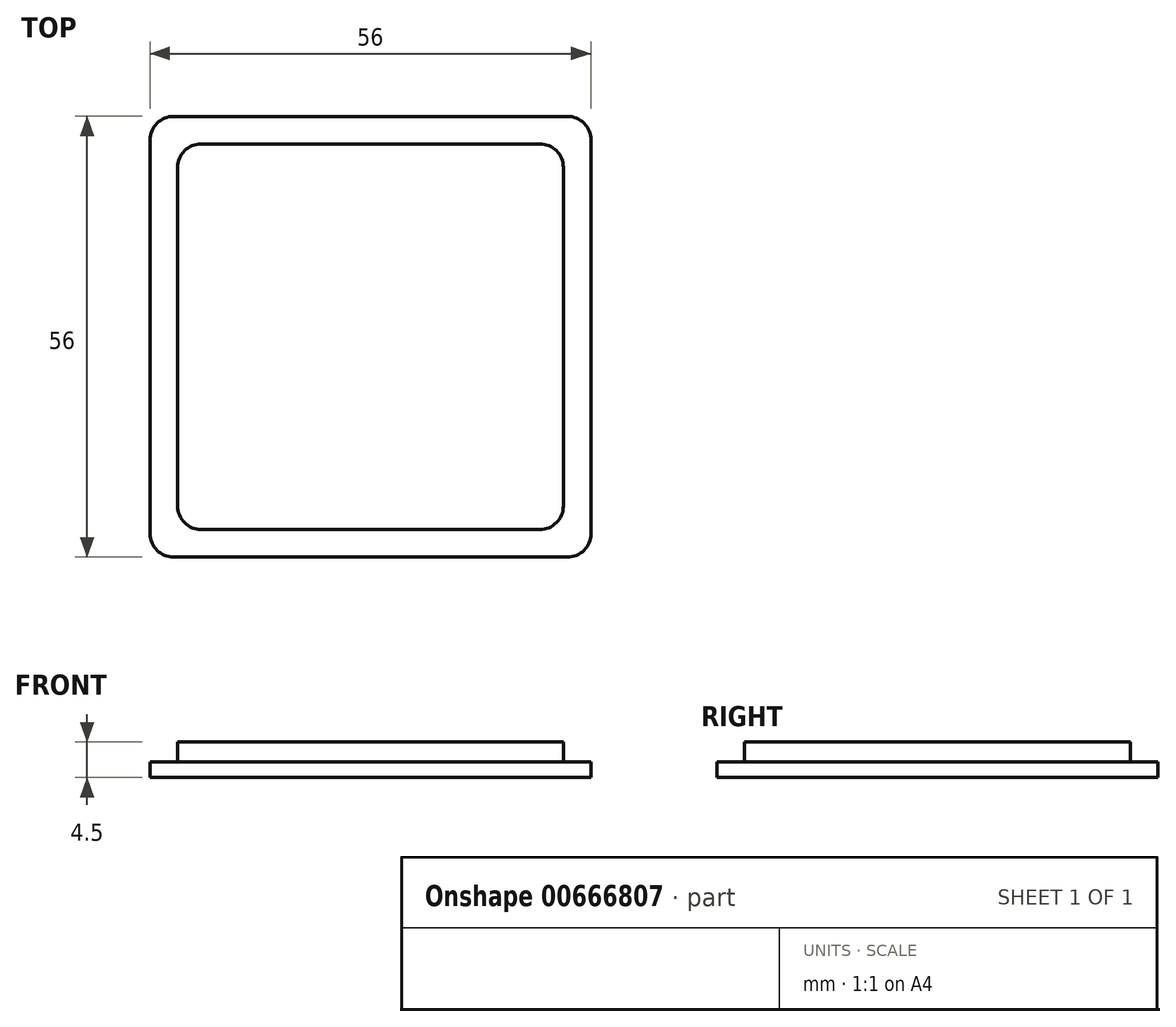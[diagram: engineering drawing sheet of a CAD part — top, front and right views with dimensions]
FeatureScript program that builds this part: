
annotation { "Feature Type Name" : "Feature", "Feature Type Description" : "" }
export const myFeature = defineFeature(function(context is Context, id is Id, definition is map)
    precondition{}
    {
        {
            var Q0;
            Q0=qCreatedBy(makeId("Top.planeOp"),FACE);
            var sketch = newSketch(context, id + "F0", { "sketchPlane" : qUnion([Q0])});
            skLineSegment(sketch, "E0.bottom", {"start": v(-28.93, 29.36) * mm, "end": v(21.07, 29.36) * mm});
            skLineSegment(sketch, "E0.top", {"start": v(-28.93, -26.64) * mm, "end": v(21.07, -26.64) * mm});
            skLineSegment(sketch, "E0.left", {"start": v(-31.93, 26.36) * mm, "end": v(-31.93, -23.64) * mm});
            skLineSegment(sketch, "E0.right", {"start": v(24.07, 26.36) * mm, "end": v(24.07, -23.64) * mm});
            skPoint(sketch, "E1.visualSharp", {"position": v(-31.93, 29.36) * mm});
            skArc(sketch, "E1.filletArc", {"start": v(-28.93, 29.36) * mm, "mid": v(-31.05, 28.48) * mm, "end": v(-31.93, 26.36) * mm});
            skPoint(sketch, "E2.visualSharp", {"position": v(24.07, 29.36) * mm});
            skArc(sketch, "E2.filletArc", {"start": v(24.07, 26.36) * mm, "mid": v(23.2, 28.48) * mm, "end": v(21.07, 29.36) * mm});
            skPoint(sketch, "E3.visualSharp", {"position": v(24.07, -26.64) * mm});
            skArc(sketch, "E3.filletArc", {"start": v(21.07, -26.64) * mm, "mid": v(23.2, -25.76) * mm, "end": v(24.07, -23.64) * mm});
            skPoint(sketch, "E4.visualSharp", {"position": v(-31.93, -26.64) * mm});
            skArc(sketch, "E4.filletArc", {"start": v(-31.93, -23.64) * mm, "mid": v(-31.05, -25.76) * mm, "end": v(-28.93, -26.64) * mm});
            skSolve(sketch);
        }
        {
            var Q0;
            Q0=makeQuery(id+"F0.imprint","IMPRINT",FACE,{"disambiguationData":[TD([[makeQuery(id+"F0.imprint","IMPRINT",EDGE,{"derivedFrom":sQuery(id+"F0.wireOp",EDGE,"E0.bottom")}),-1.0]])]});
            extrude(context, id + "F1", {"entities" : qUnion([Q0]), "depth" : 2 * mm, "offsetDistance" : 25 * mm});
        }
        {
            var Q0;
            Q0=makeQuery(id+"F1.opExtrude","CAP_FACE",FACE,{"disambiguationData":[OSD([sQuery(id+"F0.wireOp",EDGE,"E0.bottom"),sQuery(id+"F0.wireOp",EDGE,"E0.top"),sQuery(id+"F0.wireOp",EDGE,"E0.left"),sQuery(id+"F0.wireOp",EDGE,"E0.right"),sQuery(id+"F0.wireOp",EDGE,"E1.filletArc"),sQuery(id+"F0.wireOp",EDGE,"E2.filletArc"),sQuery(id+"F0.wireOp",EDGE,"E3.filletArc"),sQuery(id+"F0.wireOp",EDGE,"E4.filletArc")])],"isStart":false});
            var sketch = newSketch(context, id + "F2", { "sketchPlane" : qUnion([Q0])});
            skLineSegment(sketch, "E5.0", {"start": v(-25.43, -23.14) * mm, "end": v(17.57, -23.14) * mm});
            skLineSegment(sketch, "E6.0", {"start": v(20.57, 22.86) * mm, "end": v(20.57, -20.14) * mm});
            skLineSegment(sketch, "E7.0", {"start": v(-25.43, 25.86) * mm, "end": v(17.57, 25.86) * mm});
            skLineSegment(sketch, "E8.0", {"start": v(-28.43, 22.86) * mm, "end": v(-28.43, -20.14) * mm});
            skPoint(sketch, "E9.visualSharp", {"position": v(-28.43, 25.86) * mm});
            skArc(sketch, "E9.filletArc", {"start": v(-25.43, 25.86) * mm, "mid": v(-27.55, 24.98) * mm, "end": v(-28.43, 22.86) * mm});
            skPoint(sketch, "E10.visualSharp", {"position": v(20.57, 25.86) * mm});
            skArc(sketch, "E10.filletArc", {"start": v(20.57, 22.86) * mm, "mid": v(19.7, 24.98) * mm, "end": v(17.57, 25.86) * mm});
            skPoint(sketch, "E11.visualSharp", {"position": v(20.57, -23.14) * mm});
            skArc(sketch, "E11.filletArc", {"start": v(17.57, -23.14) * mm, "mid": v(19.7, -22.26) * mm, "end": v(20.57, -20.14) * mm});
            skPoint(sketch, "E12.visualSharp", {"position": v(-28.43, -23.14) * mm});
            skArc(sketch, "E12.filletArc", {"start": v(-28.43, -20.14) * mm, "mid": v(-27.55, -22.26) * mm, "end": v(-25.43, -23.14) * mm});
            skSolve(sketch);
        }
        {
            var Q0;
            Q0=makeQuery(id+"F2.imprint","IMPRINT",FACE,{"disambiguationData":[TD([[makeQuery(id+"F2.imprint","IMPRINT",EDGE,{"derivedFrom":sQuery(id+"F2.wireOp",EDGE,"E5.0")}),1.0]])]});
            extrude(context, id + "F3", {"entities" : qUnion([Q0]), "operationType" : NewBodyOperationType.ADD, "depth" : 2.5 * mm, "offsetDistance" : 25 * mm});
        }
    });
